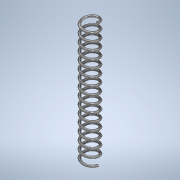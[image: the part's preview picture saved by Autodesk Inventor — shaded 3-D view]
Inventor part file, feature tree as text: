
AUTODESK INVENTOR PART (.ipt)
format: ipt  version: 2021 (Build 250183000, 183)  size: 291,328 bytes
history: native  units: mm
features: other x2, sketch x1
ambient origin geometry x8: Origin, YZ Plane, XZ Plane, XY Plane, X Axis, Y Axis, Z Axis, Center Point
bodies: Body1 (feature_tree)
feature tree (3):
  other  "Sólido1"
  other  "Espiral1"
  sketch  "Esboço1"  dims[d0=1.8mm d1=2.5mm d2=0.35mm d3=10.0mm d4=18.0mm d5=160.0mm d6=0.0mm d7=90.0deg d8=90.0deg d9=0.0mm d10=0.0mm]
